# Revit family: Urinal-Wall_Mount-KOHLER-Tend-K-28080T_1
name_source: partatom
category: Plumbing Fixtures
units: mm (PartAtom-declared; Revit-internal decimal feet)

## family parameters
Cut with Voids When Loaded = No
Host = Face
Maintain Annotation Orientation = No
OmniClass Number = 23.31.21.00
OmniClass Title = Urinals
Part Type = Normal
Room Calculation Point = No
Round Connector Dimension = Use Diameter
Shared = No

## types (3) — shared parameters
ADA Compliant = No
Assembly Code = D2010200
CW Connection = Yes
Cold Water Inlet = Cold Water Inlet
Date Modified = 05/12/2022
Default Elevation = 0"
Finish = Kohler-Vitreous_China-0-White
Flow Rate = 0 GPM
HW Connection = No
Height = 28 3/16"
Hot Water Inlet = Hot Water Inlet
Length = 14 5/8"
Manufacturer = Kohler Co.
Master Format 2014 = 22 41 13.16
Master Format 2014 Name = Residential Urinals
Material = Vitreous China
Pressure = 0.00 psi
Product Name = Tend
URL = http://www.kohler.com.cn
Vent Connection = No
Waste Connection = Yes
Waste Water Outlet = Waste Water Outlet
WaterSense Certified = No
Width = 13 5/8"

## per-type parameters (varying)
| type | Description | Flush Rate- GPF | Flush Rate- LPF | Model | Type |
| 2.5 LPF, 0-White | WALL HUNG 1/2 STL T-LESS URINAL 2.5L | 0.66GPF | 2.5 LPF | K-28080T-0 | 1 |
| 0.5 LPF and ECO, 0-White | WALL HUNG 1/2 STL ECO T-LESS URINAL 0.5L | 0.13GPF | 0.5 LPF | K-28080T-Y-0 | 2 |
| 0.5 LPF, 0-White | WALL HUNG 1/2 STL T-LESS URINAL IOT 0.5L | 0.13GPF | 0.5 LPF | K-28080T-XY-0 | 3 |

## geometry (parser evidence)
native form markers: Sweep x5
no freeform markers — native parametric forms only
